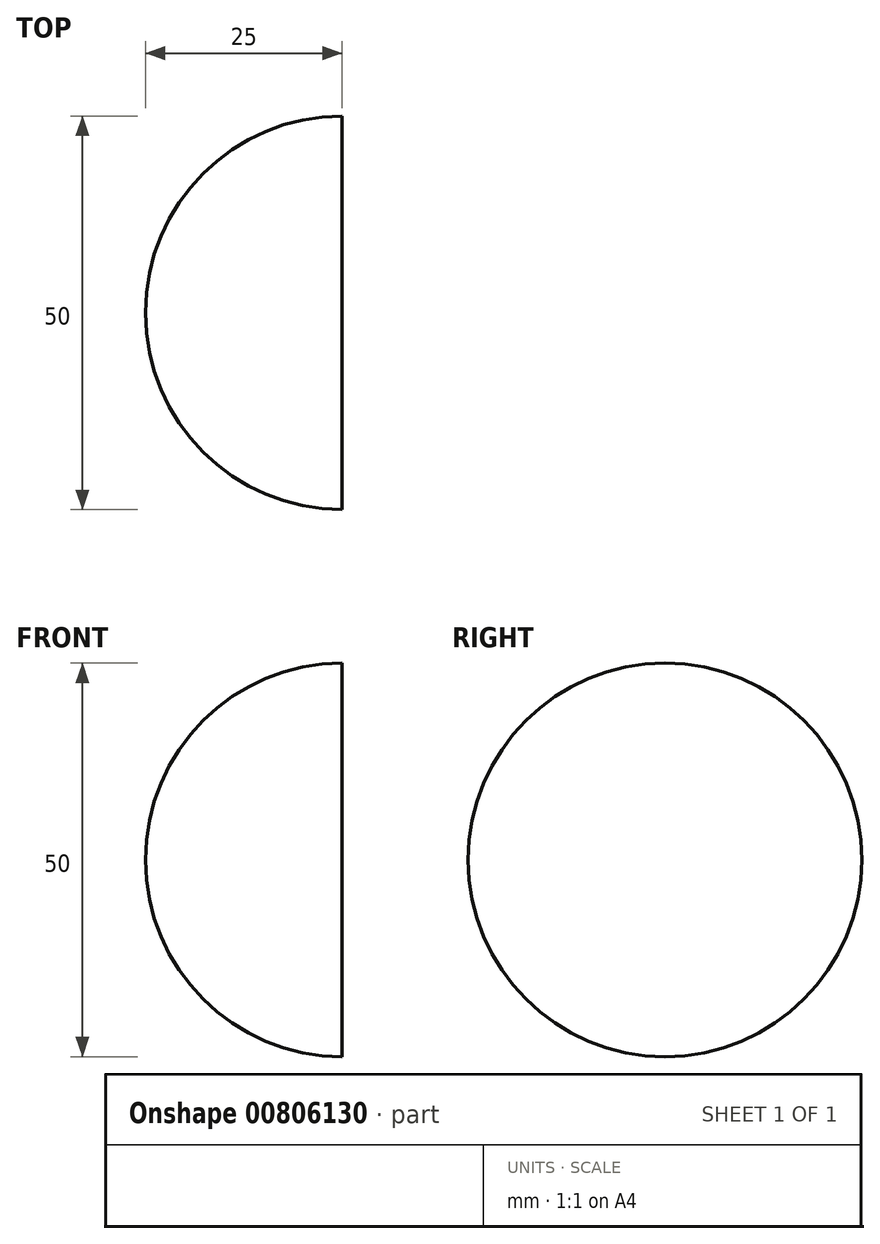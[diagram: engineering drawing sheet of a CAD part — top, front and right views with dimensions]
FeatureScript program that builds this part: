
annotation { "Feature Type Name" : "Feature", "Feature Type Description" : "" }
export const myFeature = defineFeature(function(context is Context, id is Id, definition is map)
    precondition{}
    {
        {
            var Q0;
            Q0=qCreatedBy(makeId("Right.planeOp"),FACE);
            var sketch = newSketch(context, id + "F0", { "sketchPlane" : qUnion([Q0])});
            skArc(sketch, "E0", {"start": v(0, 25) * mm, "mid": v(-25, 0) * mm, "end": v(0, -25) * mm});
            skLineSegment(sketch, "E1", {"start": v(0, 25) * mm, "end": v(0, -25) * mm});
            skSolve(sketch);
        }
        {
            var Q0;
            Q0=makeQuery(id+"F0.imprint","IMPRINT",FACE,{"disambiguationData":[TD([[makeQuery(id+"F0.imprint","IMPRINT",EDGE,{"derivedFrom":sQuery(id+"F0.wireOp",EDGE,"E0")}),1.0]])]});
            var Q1;
            Q1=sQuery(id+"F0.wireOp",EDGE,"E0");
            var Q2;
            Q2=sQuery(id+"F0.wireOp",EDGE,"E1");
            revolve(context, id + "F1", {"surfaceOperationType" : NewSurfaceOperationType.NEW, "entities" : qUnion([Q0]), "surfaceEntities" : qUnion([Q1]), "axis" : qUnion([Q2]), "revolveType" : RevolveType.ONE_DIRECTION, "angle" : 180 * degree});
        }
    });
